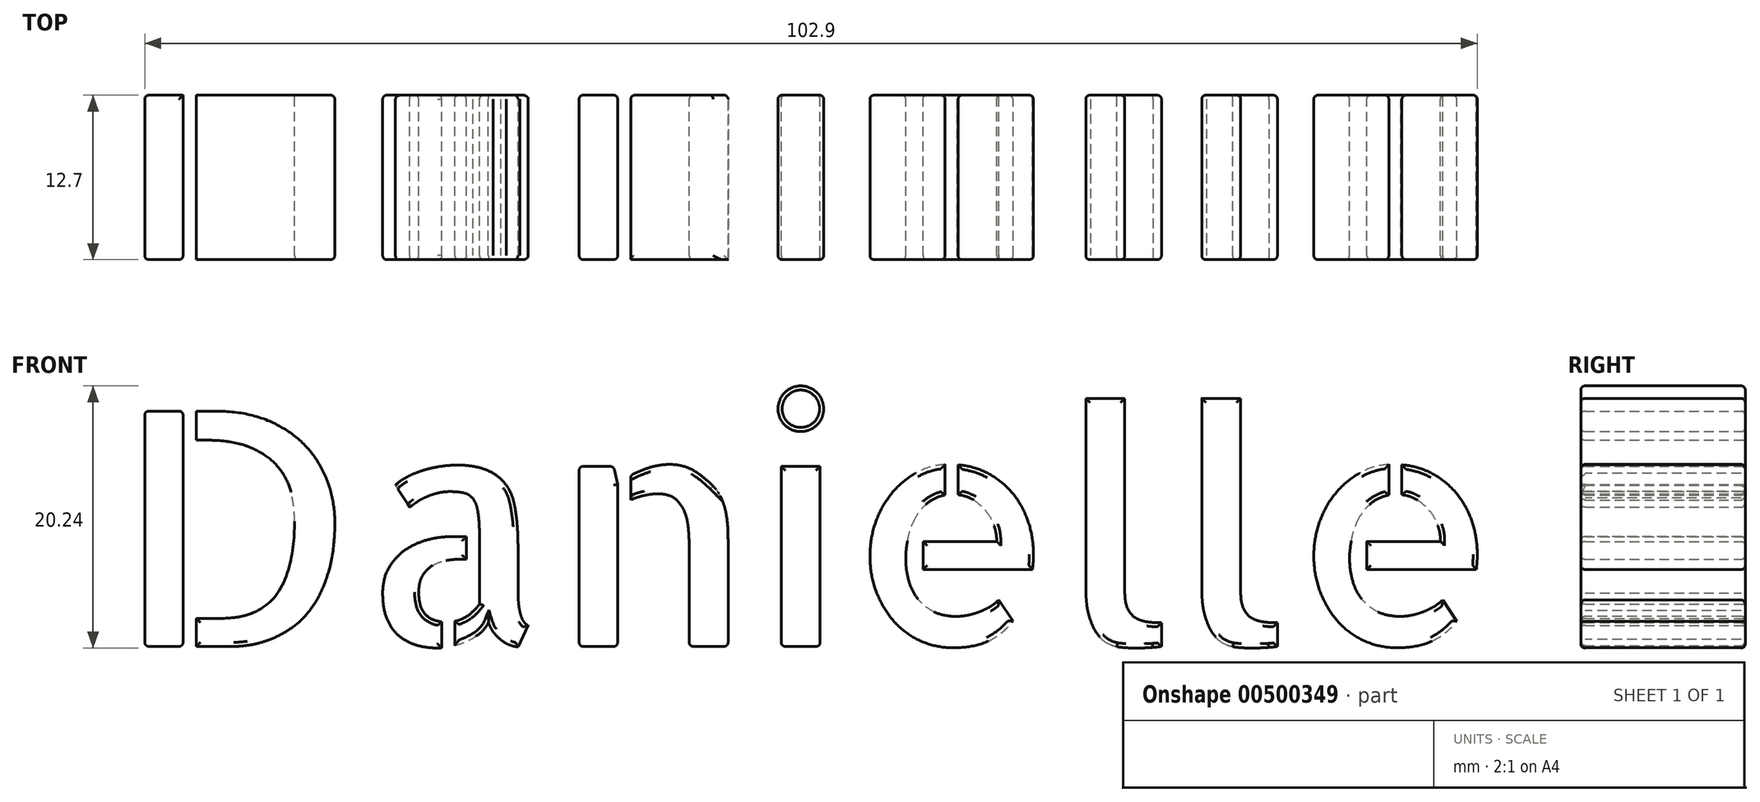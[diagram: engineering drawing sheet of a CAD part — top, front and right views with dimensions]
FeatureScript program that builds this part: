
annotation { "Feature Type Name" : "Feature", "Feature Type Description" : "" }
export const myFeature = defineFeature(function(context is Context, id is Id, definition is map)
    precondition{}
    {
        {
            var Q0;
            Q0=qCreatedBy(makeId("Front.planeOp"),FACE);
            var sketch = newSketch(context, id + "F0", { "sketchPlane" : qUnion([Q0])});
            skText(sketch, "E0", { "text": "Danielle", "fontName": "AllertaStencil-Regular.ttf"});
            const initialGuessF0  = {"E0": [-0.06588, 0.00923, 1, 0, 0.01818]};
            skSetInitialGuess(sketch, initialGuessF0);
            skSolve(sketch);
        }
        {
            var Q0;
            Q0 = qSketchRegion(id + "F0", true);
            extrude(context, id + "F1", {"entities" : qUnion([Q0]), "depth" : 12.7 * mm});
        }
        {
            var Q0;
            Q0=makeQuery(id+"F1.opExtrude","CAP_EDGE",EDGE,{"disambiguationData":[OSD([sQuery(id+"F0.wireOp",EDGE,"E0.sketch_text.stroke-3")])],"isStart":false});
            var Q1;
            Q1=makeQuery(id+"F1.opExtrude","CAP_EDGE",EDGE,{"disambiguationData":[OSD([sQuery(id+"F0.wireOp",EDGE,"E0.sketch_text.stroke-32")])],"isStart":false});
            var Q2;
            Q2=makeQuery(id+"F1.opExtrude","CAP_EDGE",EDGE,{"disambiguationData":[OSD([sQuery(id+"F0.wireOp",EDGE,"E0.sketch_text.stroke-60")])],"isStart":false});
            var Q3;
            Q3=makeQuery(id+"F1.opExtrude","CAP_EDGE",EDGE,{"disambiguationData":[OSD([sQuery(id+"F0.wireOp",EDGE,"E0.sketch_text.stroke-57")])],"isStart":false});
            var Q4;
            Q4=makeQuery(id+"F1.opExtrude","CAP_EDGE",EDGE,{"disambiguationData":[OSD([sQuery(id+"F0.wireOp",EDGE,"E0.sketch_text.stroke-56")])],"isStart":false});
            var Q5;
            Q5=makeQuery(id+"F1.opExtrude","CAP_EDGE",EDGE,{"disambiguationData":[OSD([sQuery(id+"F0.wireOp",EDGE,"E0.sketch_text.stroke-55")])],"isStart":false});
            var Q6;
            Q6=makeQuery(id+"F1.opExtrude","CAP_EDGE",EDGE,{"disambiguationData":[OSD([sQuery(id+"F0.wireOp",EDGE,"E0.sketch_text.stroke-52")])],"isStart":false});
            var Q7;
            Q7=makeQuery(id+"F1.opExtrude","CAP_EDGE",EDGE,{"disambiguationData":[OSD([sQuery(id+"F0.wireOp",EDGE,"E0.sketch_text.stroke-45")])],"isStart":false});
            var Q8;
            Q8=makeQuery(id+"F1.opExtrude","CAP_EDGE",EDGE,{"disambiguationData":[OSD([sQuery(id+"F0.wireOp",EDGE,"E0.sketch_text.stroke-49")])],"isStart":false});
            var Q9;
            Q9=makeQuery(id+"F1.opExtrude","CAP_EDGE",EDGE,{"disambiguationData":[OSD([sQuery(id+"F0.wireOp",EDGE,"E0.sketch_text.stroke-42")])],"isStart":false});
            var Q10;
            Q10=makeQuery(id+"F1.opExtrude","CAP_EDGE",EDGE,{"disambiguationData":[OSD([sQuery(id+"F0.wireOp",EDGE,"E0.sketch_text.stroke-28")])],"isStart":false});
            var Q11;
            Q11=makeQuery(id+"F1.opExtrude","CAP_FACE",FACE,{"disambiguationData":[OSD([sQuery(id+"F0.wireOp",EDGE,"E0.sketch_text.stroke-26"),sQuery(id+"F0.wireOp",EDGE,"E0.sketch_text.stroke-27"),sQuery(id+"F0.wireOp",EDGE,"E0.sketch_text.stroke-28"),sQuery(id+"F0.wireOp",EDGE,"E0.sketch_text.stroke-29"),sQuery(id+"F0.wireOp",EDGE,"E0.sketch_text.stroke-30"),sQuery(id+"F0.wireOp",EDGE,"E0.sketch_text.stroke-31"),sQuery(id+"F0.wireOp",EDGE,"E0.sketch_text.stroke-32"),sQuery(id+"F0.wireOp",EDGE,"E0.sketch_text.stroke-33"),sQuery(id+"F0.wireOp",EDGE,"E0.sketch_text.stroke-34"),sQuery(id+"F0.wireOp",EDGE,"E0.sketch_text.stroke-35"),sQuery(id+"F0.wireOp",EDGE,"E0.sketch_text.stroke-36"),sQuery(id+"F0.wireOp",EDGE,"E0.sketch_text.stroke-37"),sQuery(id+"F0.wireOp",EDGE,"E0.sketch_text.stroke-38"),sQuery(id+"F0.wireOp",EDGE,"E0.sketch_text.stroke-39"),sQuery(id+"F0.wireOp",EDGE,"E0.sketch_text.stroke-40"),sQuery(id+"F0.wireOp",EDGE,"E0.sketch_text.stroke-41"),sQuery(id+"F0.wireOp",EDGE,"E0.sketch_text.stroke-42"),sQuery(id+"F0.wireOp",EDGE,"E0.sketch_text.stroke-43"),sQuery(id+"F0.wireOp",EDGE,"E0.sketch_text.stroke-44")])],"isStart":false});
            var Q12;
            Q12=makeQuery(id+"F1.opExtrude","CAP_EDGE",EDGE,{"disambiguationData":[OSD([sQuery(id+"F0.wireOp",EDGE,"E0.sketch_text.stroke-83")])],"isStart":false});
            var Q13;
            Q13=makeQuery(id+"F1.opExtrude","CAP_EDGE",EDGE,{"disambiguationData":[OSD([sQuery(id+"F0.wireOp",EDGE,"E0.sketch_text.stroke-84")])],"isStart":false});
            var Q14;
            Q14=makeQuery(id+"F1.opExtrude","CAP_EDGE",EDGE,{"disambiguationData":[OSD([sQuery(id+"F0.wireOp",EDGE,"E0.sketch_text.stroke-9")])],"isStart":false});
            var Q15;
            Q15=makeQuery(id+"F1.opExtrude","CAP_EDGE",EDGE,{"disambiguationData":[OSD([sQuery(id+"F0.wireOp",EDGE,"E0.sketch_text.stroke-18")])],"isStart":false});
            var Q16;
            Q16=makeQuery(id+"F1.opExtrude","CAP_EDGE",EDGE,{"disambiguationData":[OSD([sQuery(id+"F0.wireOp",EDGE,"E0.sketch_text.stroke-15")])],"isStart":false});
            var Q17;
            Q17=makeQuery(id+"F1.opExtrude","CAP_EDGE",EDGE,{"disambiguationData":[OSD([sQuery(id+"F0.wireOp",EDGE,"E0.sketch_text.stroke-82")])],"isStart":false});
            var Q18;
            Q18=makeQuery(id+"F1.opExtrude","SWEPT_FACE",FACE,{"disambiguationData":[OSD([sQuery(id+"F0.wireOp",EDGE,"E0.sketch_text.stroke-85")])]});
            var Q19;
            Q19=makeQuery(id+"F1.opExtrude","CAP_EDGE",EDGE,{"disambiguationData":[OSD([sQuery(id+"F0.wireOp",EDGE,"E0.sketch_text.stroke-81")])],"isStart":false});
            var Q20;
            Q20=makeQuery(id+"F1.opExtrude","SWEPT_EDGE",EDGE,{"disambiguationData":[OSD([sQuery(id+"F0.wireOp",EDGE,"E0.sketch_text.stroke-100"),sQuery(id+"F0.wireOp",EDGE,"E0.sketch_text.stroke-101")])]});
            var Q21;
            Q21=makeQuery(id+"F1.opExtrude","CAP_EDGE",EDGE,{"disambiguationData":[OSD([sQuery(id+"F0.wireOp",EDGE,"E0.sketch_text.stroke-103")])],"isStart":false});
            var Q22;
            Q22=makeQuery(id+"F1.opExtrude","CAP_EDGE",EDGE,{"disambiguationData":[OSD([sQuery(id+"F0.wireOp",EDGE,"E0.sketch_text.stroke-98")])],"isStart":false});
            var Q23;
            Q23=makeQuery(id+"F1.opExtrude","CAP_EDGE",EDGE,{"disambiguationData":[OSD([sQuery(id+"F0.wireOp",EDGE,"E0.sketch_text.stroke-92")])],"isStart":false});
            var Q24;
            Q24=makeQuery(id+"F1.opExtrude","CAP_EDGE",EDGE,{"disambiguationData":[OSD([sQuery(id+"F0.wireOp",EDGE,"E0.sketch_text.stroke-106")])],"isStart":false});
            var Q25;
            Q25=makeQuery(id+"F1.opExtrude","CAP_EDGE",EDGE,{"disambiguationData":[OSD([sQuery(id+"F0.wireOp",EDGE,"E0.sketch_text.stroke-107")])],"isStart":false});
            var Q26;
            Q26=makeQuery(id+"F1.opExtrude","CAP_EDGE",EDGE,{"disambiguationData":[OSD([sQuery(id+"F0.wireOp",EDGE,"E0.sketch_text.stroke-110")])],"isStart":false});
            var Q27;
            Q27=makeQuery(id+"F1.opExtrude","CAP_FACE",FACE,{"disambiguationData":[OSD([sQuery(id+"F0.wireOp",EDGE,"E0.sketch_text.stroke-109"),sQuery(id+"F0.wireOp",EDGE,"E0.sketch_text.stroke-110"),sQuery(id+"F0.wireOp",EDGE,"E0.sketch_text.stroke-111"),sQuery(id+"F0.wireOp",EDGE,"E0.sketch_text.stroke-112"),sQuery(id+"F0.wireOp",EDGE,"E0.sketch_text.stroke-113"),sQuery(id+"F0.wireOp",EDGE,"E0.sketch_text.stroke-114"),sQuery(id+"F0.wireOp",EDGE,"E0.sketch_text.stroke-115"),sQuery(id+"F0.wireOp",EDGE,"E0.sketch_text.stroke-116")])],"isStart":false});
            var Q28;
            Q28=makeQuery(id+"F1.opExtrude","CAP_FACE",FACE,{"disambiguationData":[OSD([sQuery(id+"F0.wireOp",EDGE,"E0.sketch_text.stroke-130"),sQuery(id+"F0.wireOp",EDGE,"E0.sketch_text.stroke-131"),sQuery(id+"F0.wireOp",EDGE,"E0.sketch_text.stroke-132"),sQuery(id+"F0.wireOp",EDGE,"E0.sketch_text.stroke-133"),sQuery(id+"F0.wireOp",EDGE,"E0.sketch_text.stroke-134"),sQuery(id+"F0.wireOp",EDGE,"E0.sketch_text.stroke-135"),sQuery(id+"F0.wireOp",EDGE,"E0.sketch_text.stroke-136"),sQuery(id+"F0.wireOp",EDGE,"E0.sketch_text.stroke-137"),sQuery(id+"F0.wireOp",EDGE,"E0.sketch_text.stroke-138"),sQuery(id+"F0.wireOp",EDGE,"E0.sketch_text.stroke-139"),sQuery(id+"F0.wireOp",EDGE,"E0.sketch_text.stroke-140"),sQuery(id+"F0.wireOp",EDGE,"E0.sketch_text.stroke-141"),sQuery(id+"F0.wireOp",EDGE,"E0.sketch_text.stroke-142"),sQuery(id+"F0.wireOp",EDGE,"E0.sketch_text.stroke-143"),sQuery(id+"F0.wireOp",EDGE,"E0.sketch_text.stroke-144"),sQuery(id+"F0.wireOp",EDGE,"E0.sketch_text.stroke-145"),sQuery(id+"F0.wireOp",EDGE,"E0.sketch_text.stroke-146"),sQuery(id+"F0.wireOp",EDGE,"E0.sketch_text.stroke-147"),sQuery(id+"F0.wireOp",EDGE,"E0.sketch_text.stroke-148"),sQuery(id+"F0.wireOp",EDGE,"E0.sketch_text.stroke-149"),sQuery(id+"F0.wireOp",EDGE,"E0.sketch_text.stroke-150"),sQuery(id+"F0.wireOp",EDGE,"E0.sketch_text.stroke-151"),sQuery(id+"F0.wireOp",EDGE,"E0.sketch_text.stroke-152"),sQuery(id+"F0.wireOp",EDGE,"E0.sketch_text.stroke-153")])],"isStart":false});
            var Q29;
            Q29=makeQuery(id+"F1.opExtrude","CAP_FACE",FACE,{"disambiguationData":[OSD([sQuery(id+"F0.wireOp",EDGE,"E0.sketch_text.stroke-117"),sQuery(id+"F0.wireOp",EDGE,"E0.sketch_text.stroke-118"),sQuery(id+"F0.wireOp",EDGE,"E0.sketch_text.stroke-119"),sQuery(id+"F0.wireOp",EDGE,"E0.sketch_text.stroke-120"),sQuery(id+"F0.wireOp",EDGE,"E0.sketch_text.stroke-121"),sQuery(id+"F0.wireOp",EDGE,"E0.sketch_text.stroke-122"),sQuery(id+"F0.wireOp",EDGE,"E0.sketch_text.stroke-123"),sQuery(id+"F0.wireOp",EDGE,"E0.sketch_text.stroke-124"),sQuery(id+"F0.wireOp",EDGE,"E0.sketch_text.stroke-125"),sQuery(id+"F0.wireOp",EDGE,"E0.sketch_text.stroke-126"),sQuery(id+"F0.wireOp",EDGE,"E0.sketch_text.stroke-127"),sQuery(id+"F0.wireOp",EDGE,"E0.sketch_text.stroke-128"),sQuery(id+"F0.wireOp",EDGE,"E0.sketch_text.stroke-129")])],"isStart":false});
            var Q30;
            Q30=makeQuery(id+"F1.opExtrude","CAP_FACE",FACE,{"disambiguationData":[OSD([sQuery(id+"F0.wireOp",EDGE,"E0.sketch_text.stroke-0"),sQuery(id+"F0.wireOp",EDGE,"E0.sketch_text.stroke-1"),sQuery(id+"F0.wireOp",EDGE,"E0.sketch_text.stroke-2"),sQuery(id+"F0.wireOp",EDGE,"E0.sketch_text.stroke-3")])],"isStart":false});
            var Q31;
            Q31=makeQuery(id+"F1.opExtrude","SWEPT_FACE",FACE,{"disambiguationData":[OSD([sQuery(id+"F0.wireOp",EDGE,"E0.sketch_text.stroke-0")])]});
            var Q32;
            Q32=makeQuery(id+"F1.opExtrude","CAP_FACE",FACE,{"disambiguationData":[OSD([sQuery(id+"F0.wireOp",EDGE,"E0.sketch_text.stroke-154"),sQuery(id+"F0.wireOp",EDGE,"E0.sketch_text.stroke-155"),sQuery(id+"F0.wireOp",EDGE,"E0.sketch_text.stroke-156"),sQuery(id+"F0.wireOp",EDGE,"E0.sketch_text.stroke-157"),sQuery(id+"F0.wireOp",EDGE,"E0.sketch_text.stroke-158"),sQuery(id+"F0.wireOp",EDGE,"E0.sketch_text.stroke-159"),sQuery(id+"F0.wireOp",EDGE,"E0.sketch_text.stroke-160"),sQuery(id+"F0.wireOp",EDGE,"E0.sketch_text.stroke-161"),sQuery(id+"F0.wireOp",EDGE,"E0.sketch_text.stroke-162"),sQuery(id+"F0.wireOp",EDGE,"E0.sketch_text.stroke-163"),sQuery(id+"F0.wireOp",EDGE,"E0.sketch_text.stroke-164"),sQuery(id+"F0.wireOp",EDGE,"E0.sketch_text.stroke-165"),sQuery(id+"F0.wireOp",EDGE,"E0.sketch_text.stroke-166"),sQuery(id+"F0.wireOp",EDGE,"E0.sketch_text.stroke-167"),sQuery(id+"F0.wireOp",EDGE,"E0.sketch_text.stroke-168"),sQuery(id+"F0.wireOp",EDGE,"E0.sketch_text.stroke-169"),sQuery(id+"F0.wireOp",EDGE,"E0.sketch_text.stroke-170"),sQuery(id+"F0.wireOp",EDGE,"E0.sketch_text.stroke-171")])],"isStart":false});
            var Q33;
            Q33=makeQuery(id+"F1.opExtrude","CAP_FACE",FACE,{"disambiguationData":[OSD([sQuery(id+"F0.wireOp",EDGE,"E0.sketch_text.stroke-172"),sQuery(id+"F0.wireOp",EDGE,"E0.sketch_text.stroke-173"),sQuery(id+"F0.wireOp",EDGE,"E0.sketch_text.stroke-174"),sQuery(id+"F0.wireOp",EDGE,"E0.sketch_text.stroke-175"),sQuery(id+"F0.wireOp",EDGE,"E0.sketch_text.stroke-176"),sQuery(id+"F0.wireOp",EDGE,"E0.sketch_text.stroke-177"),sQuery(id+"F0.wireOp",EDGE,"E0.sketch_text.stroke-178"),sQuery(id+"F0.wireOp",EDGE,"E0.sketch_text.stroke-179"),sQuery(id+"F0.wireOp",EDGE,"E0.sketch_text.stroke-180"),sQuery(id+"F0.wireOp",EDGE,"E0.sketch_text.stroke-181"),sQuery(id+"F0.wireOp",EDGE,"E0.sketch_text.stroke-182"),sQuery(id+"F0.wireOp",EDGE,"E0.sketch_text.stroke-183"),sQuery(id+"F0.wireOp",EDGE,"E0.sketch_text.stroke-184"),sQuery(id+"F0.wireOp",EDGE,"E0.sketch_text.stroke-185"),sQuery(id+"F0.wireOp",EDGE,"E0.sketch_text.stroke-186"),sQuery(id+"F0.wireOp",EDGE,"E0.sketch_text.stroke-187"),sQuery(id+"F0.wireOp",EDGE,"E0.sketch_text.stroke-188"),sQuery(id+"F0.wireOp",EDGE,"E0.sketch_text.stroke-189")])],"isStart":false});
            var Q34;
            Q34=makeQuery(id+"F1.opExtrude","CAP_FACE",FACE,{"disambiguationData":[OSD([sQuery(id+"F0.wireOp",EDGE,"E0.sketch_text.stroke-203"),sQuery(id+"F0.wireOp",EDGE,"E0.sketch_text.stroke-204"),sQuery(id+"F0.wireOp",EDGE,"E0.sketch_text.stroke-205"),sQuery(id+"F0.wireOp",EDGE,"E0.sketch_text.stroke-206"),sQuery(id+"F0.wireOp",EDGE,"E0.sketch_text.stroke-207"),sQuery(id+"F0.wireOp",EDGE,"E0.sketch_text.stroke-208"),sQuery(id+"F0.wireOp",EDGE,"E0.sketch_text.stroke-209"),sQuery(id+"F0.wireOp",EDGE,"E0.sketch_text.stroke-210"),sQuery(id+"F0.wireOp",EDGE,"E0.sketch_text.stroke-211"),sQuery(id+"F0.wireOp",EDGE,"E0.sketch_text.stroke-212"),sQuery(id+"F0.wireOp",EDGE,"E0.sketch_text.stroke-213"),sQuery(id+"F0.wireOp",EDGE,"E0.sketch_text.stroke-214"),sQuery(id+"F0.wireOp",EDGE,"E0.sketch_text.stroke-215"),sQuery(id+"F0.wireOp",EDGE,"E0.sketch_text.stroke-216"),sQuery(id+"F0.wireOp",EDGE,"E0.sketch_text.stroke-217"),sQuery(id+"F0.wireOp",EDGE,"E0.sketch_text.stroke-218"),sQuery(id+"F0.wireOp",EDGE,"E0.sketch_text.stroke-219"),sQuery(id+"F0.wireOp",EDGE,"E0.sketch_text.stroke-220"),sQuery(id+"F0.wireOp",EDGE,"E0.sketch_text.stroke-221"),sQuery(id+"F0.wireOp",EDGE,"E0.sketch_text.stroke-222"),sQuery(id+"F0.wireOp",EDGE,"E0.sketch_text.stroke-223"),sQuery(id+"F0.wireOp",EDGE,"E0.sketch_text.stroke-224"),sQuery(id+"F0.wireOp",EDGE,"E0.sketch_text.stroke-225"),sQuery(id+"F0.wireOp",EDGE,"E0.sketch_text.stroke-226")])],"isStart":false});
            var Q35;
            Q35=makeQuery(id+"F1.opExtrude","CAP_FACE",FACE,{"disambiguationData":[OSD([sQuery(id+"F0.wireOp",EDGE,"E0.sketch_text.stroke-190"),sQuery(id+"F0.wireOp",EDGE,"E0.sketch_text.stroke-191"),sQuery(id+"F0.wireOp",EDGE,"E0.sketch_text.stroke-192"),sQuery(id+"F0.wireOp",EDGE,"E0.sketch_text.stroke-193"),sQuery(id+"F0.wireOp",EDGE,"E0.sketch_text.stroke-194"),sQuery(id+"F0.wireOp",EDGE,"E0.sketch_text.stroke-195"),sQuery(id+"F0.wireOp",EDGE,"E0.sketch_text.stroke-196"),sQuery(id+"F0.wireOp",EDGE,"E0.sketch_text.stroke-197"),sQuery(id+"F0.wireOp",EDGE,"E0.sketch_text.stroke-198"),sQuery(id+"F0.wireOp",EDGE,"E0.sketch_text.stroke-199"),sQuery(id+"F0.wireOp",EDGE,"E0.sketch_text.stroke-200"),sQuery(id+"F0.wireOp",EDGE,"E0.sketch_text.stroke-201"),sQuery(id+"F0.wireOp",EDGE,"E0.sketch_text.stroke-202")])],"isStart":false});
            var Q36;
            Q36=makeQuery(id+"F1.opExtrude","CAP_FACE",FACE,{"disambiguationData":[OSD([sQuery(id+"F0.wireOp",EDGE,"E0.sketch_text.stroke-105"),sQuery(id+"F0.wireOp",EDGE,"E0.sketch_text.stroke-106"),sQuery(id+"F0.wireOp",EDGE,"E0.sketch_text.stroke-107"),sQuery(id+"F0.wireOp",EDGE,"E0.sketch_text.stroke-108")])],"isStart":false});
            var Q37;
            Q37=makeQuery(id+"F1.opExtrude","CAP_FACE",FACE,{"disambiguationData":[OSD([sQuery(id+"F0.wireOp",EDGE,"E0.sketch_text.stroke-172"),sQuery(id+"F0.wireOp",EDGE,"E0.sketch_text.stroke-173"),sQuery(id+"F0.wireOp",EDGE,"E0.sketch_text.stroke-174"),sQuery(id+"F0.wireOp",EDGE,"E0.sketch_text.stroke-175"),sQuery(id+"F0.wireOp",EDGE,"E0.sketch_text.stroke-176"),sQuery(id+"F0.wireOp",EDGE,"E0.sketch_text.stroke-177"),sQuery(id+"F0.wireOp",EDGE,"E0.sketch_text.stroke-178"),sQuery(id+"F0.wireOp",EDGE,"E0.sketch_text.stroke-179"),sQuery(id+"F0.wireOp",EDGE,"E0.sketch_text.stroke-180"),sQuery(id+"F0.wireOp",EDGE,"E0.sketch_text.stroke-181"),sQuery(id+"F0.wireOp",EDGE,"E0.sketch_text.stroke-182"),sQuery(id+"F0.wireOp",EDGE,"E0.sketch_text.stroke-183"),sQuery(id+"F0.wireOp",EDGE,"E0.sketch_text.stroke-184"),sQuery(id+"F0.wireOp",EDGE,"E0.sketch_text.stroke-185"),sQuery(id+"F0.wireOp",EDGE,"E0.sketch_text.stroke-186"),sQuery(id+"F0.wireOp",EDGE,"E0.sketch_text.stroke-187"),sQuery(id+"F0.wireOp",EDGE,"E0.sketch_text.stroke-188"),sQuery(id+"F0.wireOp",EDGE,"E0.sketch_text.stroke-189")])],"isStart":true});
            var Q38;
            Q38=makeQuery(id+"F1.opExtrude","CAP_FACE",FACE,{"disambiguationData":[OSD([sQuery(id+"F0.wireOp",EDGE,"E0.sketch_text.stroke-154"),sQuery(id+"F0.wireOp",EDGE,"E0.sketch_text.stroke-155"),sQuery(id+"F0.wireOp",EDGE,"E0.sketch_text.stroke-156"),sQuery(id+"F0.wireOp",EDGE,"E0.sketch_text.stroke-157"),sQuery(id+"F0.wireOp",EDGE,"E0.sketch_text.stroke-158"),sQuery(id+"F0.wireOp",EDGE,"E0.sketch_text.stroke-159"),sQuery(id+"F0.wireOp",EDGE,"E0.sketch_text.stroke-160"),sQuery(id+"F0.wireOp",EDGE,"E0.sketch_text.stroke-161"),sQuery(id+"F0.wireOp",EDGE,"E0.sketch_text.stroke-162"),sQuery(id+"F0.wireOp",EDGE,"E0.sketch_text.stroke-163"),sQuery(id+"F0.wireOp",EDGE,"E0.sketch_text.stroke-164"),sQuery(id+"F0.wireOp",EDGE,"E0.sketch_text.stroke-165"),sQuery(id+"F0.wireOp",EDGE,"E0.sketch_text.stroke-166"),sQuery(id+"F0.wireOp",EDGE,"E0.sketch_text.stroke-167"),sQuery(id+"F0.wireOp",EDGE,"E0.sketch_text.stroke-168"),sQuery(id+"F0.wireOp",EDGE,"E0.sketch_text.stroke-169"),sQuery(id+"F0.wireOp",EDGE,"E0.sketch_text.stroke-170"),sQuery(id+"F0.wireOp",EDGE,"E0.sketch_text.stroke-171")])],"isStart":true});
            var Q39;
            Q39=makeQuery(id+"F1.opExtrude","CAP_FACE",FACE,{"disambiguationData":[OSD([sQuery(id+"F0.wireOp",EDGE,"E0.sketch_text.stroke-203"),sQuery(id+"F0.wireOp",EDGE,"E0.sketch_text.stroke-204"),sQuery(id+"F0.wireOp",EDGE,"E0.sketch_text.stroke-205"),sQuery(id+"F0.wireOp",EDGE,"E0.sketch_text.stroke-206"),sQuery(id+"F0.wireOp",EDGE,"E0.sketch_text.stroke-207"),sQuery(id+"F0.wireOp",EDGE,"E0.sketch_text.stroke-208"),sQuery(id+"F0.wireOp",EDGE,"E0.sketch_text.stroke-209"),sQuery(id+"F0.wireOp",EDGE,"E0.sketch_text.stroke-210"),sQuery(id+"F0.wireOp",EDGE,"E0.sketch_text.stroke-211"),sQuery(id+"F0.wireOp",EDGE,"E0.sketch_text.stroke-212"),sQuery(id+"F0.wireOp",EDGE,"E0.sketch_text.stroke-213"),sQuery(id+"F0.wireOp",EDGE,"E0.sketch_text.stroke-214"),sQuery(id+"F0.wireOp",EDGE,"E0.sketch_text.stroke-215"),sQuery(id+"F0.wireOp",EDGE,"E0.sketch_text.stroke-216"),sQuery(id+"F0.wireOp",EDGE,"E0.sketch_text.stroke-217"),sQuery(id+"F0.wireOp",EDGE,"E0.sketch_text.stroke-218"),sQuery(id+"F0.wireOp",EDGE,"E0.sketch_text.stroke-219"),sQuery(id+"F0.wireOp",EDGE,"E0.sketch_text.stroke-220"),sQuery(id+"F0.wireOp",EDGE,"E0.sketch_text.stroke-221"),sQuery(id+"F0.wireOp",EDGE,"E0.sketch_text.stroke-222"),sQuery(id+"F0.wireOp",EDGE,"E0.sketch_text.stroke-223"),sQuery(id+"F0.wireOp",EDGE,"E0.sketch_text.stroke-224"),sQuery(id+"F0.wireOp",EDGE,"E0.sketch_text.stroke-225"),sQuery(id+"F0.wireOp",EDGE,"E0.sketch_text.stroke-226")])],"isStart":true});
            var Q40;
            Q40=makeQuery(id+"F1.opExtrude","CAP_FACE",FACE,{"disambiguationData":[OSD([sQuery(id+"F0.wireOp",EDGE,"E0.sketch_text.stroke-190"),sQuery(id+"F0.wireOp",EDGE,"E0.sketch_text.stroke-191"),sQuery(id+"F0.wireOp",EDGE,"E0.sketch_text.stroke-192"),sQuery(id+"F0.wireOp",EDGE,"E0.sketch_text.stroke-193"),sQuery(id+"F0.wireOp",EDGE,"E0.sketch_text.stroke-194"),sQuery(id+"F0.wireOp",EDGE,"E0.sketch_text.stroke-195"),sQuery(id+"F0.wireOp",EDGE,"E0.sketch_text.stroke-196"),sQuery(id+"F0.wireOp",EDGE,"E0.sketch_text.stroke-197"),sQuery(id+"F0.wireOp",EDGE,"E0.sketch_text.stroke-198"),sQuery(id+"F0.wireOp",EDGE,"E0.sketch_text.stroke-199"),sQuery(id+"F0.wireOp",EDGE,"E0.sketch_text.stroke-200"),sQuery(id+"F0.wireOp",EDGE,"E0.sketch_text.stroke-201"),sQuery(id+"F0.wireOp",EDGE,"E0.sketch_text.stroke-202")])],"isStart":true});
            var Q41;
            Q41=makeQuery(id+"F1.opExtrude","CAP_FACE",FACE,{"disambiguationData":[OSD([sQuery(id+"F0.wireOp",EDGE,"E0.sketch_text.stroke-117"),sQuery(id+"F0.wireOp",EDGE,"E0.sketch_text.stroke-118"),sQuery(id+"F0.wireOp",EDGE,"E0.sketch_text.stroke-119"),sQuery(id+"F0.wireOp",EDGE,"E0.sketch_text.stroke-120"),sQuery(id+"F0.wireOp",EDGE,"E0.sketch_text.stroke-121"),sQuery(id+"F0.wireOp",EDGE,"E0.sketch_text.stroke-122"),sQuery(id+"F0.wireOp",EDGE,"E0.sketch_text.stroke-123"),sQuery(id+"F0.wireOp",EDGE,"E0.sketch_text.stroke-124"),sQuery(id+"F0.wireOp",EDGE,"E0.sketch_text.stroke-125"),sQuery(id+"F0.wireOp",EDGE,"E0.sketch_text.stroke-126"),sQuery(id+"F0.wireOp",EDGE,"E0.sketch_text.stroke-127"),sQuery(id+"F0.wireOp",EDGE,"E0.sketch_text.stroke-128"),sQuery(id+"F0.wireOp",EDGE,"E0.sketch_text.stroke-129")])],"isStart":true});
            var Q42;
            Q42=makeQuery(id+"F1.opExtrude","CAP_FACE",FACE,{"disambiguationData":[OSD([sQuery(id+"F0.wireOp",EDGE,"E0.sketch_text.stroke-130"),sQuery(id+"F0.wireOp",EDGE,"E0.sketch_text.stroke-131"),sQuery(id+"F0.wireOp",EDGE,"E0.sketch_text.stroke-132"),sQuery(id+"F0.wireOp",EDGE,"E0.sketch_text.stroke-133"),sQuery(id+"F0.wireOp",EDGE,"E0.sketch_text.stroke-134"),sQuery(id+"F0.wireOp",EDGE,"E0.sketch_text.stroke-135"),sQuery(id+"F0.wireOp",EDGE,"E0.sketch_text.stroke-136"),sQuery(id+"F0.wireOp",EDGE,"E0.sketch_text.stroke-137"),sQuery(id+"F0.wireOp",EDGE,"E0.sketch_text.stroke-138"),sQuery(id+"F0.wireOp",EDGE,"E0.sketch_text.stroke-139"),sQuery(id+"F0.wireOp",EDGE,"E0.sketch_text.stroke-140"),sQuery(id+"F0.wireOp",EDGE,"E0.sketch_text.stroke-141"),sQuery(id+"F0.wireOp",EDGE,"E0.sketch_text.stroke-142"),sQuery(id+"F0.wireOp",EDGE,"E0.sketch_text.stroke-143"),sQuery(id+"F0.wireOp",EDGE,"E0.sketch_text.stroke-144"),sQuery(id+"F0.wireOp",EDGE,"E0.sketch_text.stroke-145"),sQuery(id+"F0.wireOp",EDGE,"E0.sketch_text.stroke-146"),sQuery(id+"F0.wireOp",EDGE,"E0.sketch_text.stroke-147"),sQuery(id+"F0.wireOp",EDGE,"E0.sketch_text.stroke-148"),sQuery(id+"F0.wireOp",EDGE,"E0.sketch_text.stroke-149"),sQuery(id+"F0.wireOp",EDGE,"E0.sketch_text.stroke-150"),sQuery(id+"F0.wireOp",EDGE,"E0.sketch_text.stroke-151"),sQuery(id+"F0.wireOp",EDGE,"E0.sketch_text.stroke-152"),sQuery(id+"F0.wireOp",EDGE,"E0.sketch_text.stroke-153")])],"isStart":true});
            var Q43;
            Q43=makeQuery(id+"F1.opExtrude","CAP_FACE",FACE,{"disambiguationData":[OSD([sQuery(id+"F0.wireOp",EDGE,"E0.sketch_text.stroke-105"),sQuery(id+"F0.wireOp",EDGE,"E0.sketch_text.stroke-106"),sQuery(id+"F0.wireOp",EDGE,"E0.sketch_text.stroke-107"),sQuery(id+"F0.wireOp",EDGE,"E0.sketch_text.stroke-108")])],"isStart":true});
            var Q44;
            Q44=makeQuery(id+"F1.opExtrude","CAP_FACE",FACE,{"disambiguationData":[OSD([sQuery(id+"F0.wireOp",EDGE,"E0.sketch_text.stroke-109"),sQuery(id+"F0.wireOp",EDGE,"E0.sketch_text.stroke-110"),sQuery(id+"F0.wireOp",EDGE,"E0.sketch_text.stroke-111"),sQuery(id+"F0.wireOp",EDGE,"E0.sketch_text.stroke-112"),sQuery(id+"F0.wireOp",EDGE,"E0.sketch_text.stroke-113"),sQuery(id+"F0.wireOp",EDGE,"E0.sketch_text.stroke-114"),sQuery(id+"F0.wireOp",EDGE,"E0.sketch_text.stroke-115"),sQuery(id+"F0.wireOp",EDGE,"E0.sketch_text.stroke-116")])],"isStart":true});
            var Q45;
            Q45=makeQuery(id+"F1.opExtrude","CAP_FACE",FACE,{"disambiguationData":[OSD([sQuery(id+"F0.wireOp",EDGE,"E0.sketch_text.stroke-86"),sQuery(id+"F0.wireOp",EDGE,"E0.sketch_text.stroke-87"),sQuery(id+"F0.wireOp",EDGE,"E0.sketch_text.stroke-88"),sQuery(id+"F0.wireOp",EDGE,"E0.sketch_text.stroke-89"),sQuery(id+"F0.wireOp",EDGE,"E0.sketch_text.stroke-90"),sQuery(id+"F0.wireOp",EDGE,"E0.sketch_text.stroke-91"),sQuery(id+"F0.wireOp",EDGE,"E0.sketch_text.stroke-92"),sQuery(id+"F0.wireOp",EDGE,"E0.sketch_text.stroke-93"),sQuery(id+"F0.wireOp",EDGE,"E0.sketch_text.stroke-94"),sQuery(id+"F0.wireOp",EDGE,"E0.sketch_text.stroke-95"),sQuery(id+"F0.wireOp",EDGE,"E0.sketch_text.stroke-96"),sQuery(id+"F0.wireOp",EDGE,"E0.sketch_text.stroke-97"),sQuery(id+"F0.wireOp",EDGE,"E0.sketch_text.stroke-98"),sQuery(id+"F0.wireOp",EDGE,"E0.sketch_text.stroke-99"),sQuery(id+"F0.wireOp",EDGE,"E0.sketch_text.stroke-100"),sQuery(id+"F0.wireOp",EDGE,"E0.sketch_text.stroke-101"),sQuery(id+"F0.wireOp",EDGE,"E0.sketch_text.stroke-102"),sQuery(id+"F0.wireOp",EDGE,"E0.sketch_text.stroke-103"),sQuery(id+"F0.wireOp",EDGE,"E0.sketch_text.stroke-104")])],"isStart":true});
            var Q46;
            Q46=makeQuery(id+"F1.opExtrude","CAP_FACE",FACE,{"disambiguationData":[OSD([sQuery(id+"F0.wireOp",EDGE,"E0.sketch_text.stroke-81"),sQuery(id+"F0.wireOp",EDGE,"E0.sketch_text.stroke-82"),sQuery(id+"F0.wireOp",EDGE,"E0.sketch_text.stroke-83"),sQuery(id+"F0.wireOp",EDGE,"E0.sketch_text.stroke-84"),sQuery(id+"F0.wireOp",EDGE,"E0.sketch_text.stroke-85")])],"isStart":true});
            var Q47;
            Q47=makeQuery(id+"F1.opExtrude","CAP_FACE",FACE,{"disambiguationData":[OSD([sQuery(id+"F0.wireOp",EDGE,"E0.sketch_text.stroke-45"),sQuery(id+"F0.wireOp",EDGE,"E0.sketch_text.stroke-46"),sQuery(id+"F0.wireOp",EDGE,"E0.sketch_text.stroke-47"),sQuery(id+"F0.wireOp",EDGE,"E0.sketch_text.stroke-48"),sQuery(id+"F0.wireOp",EDGE,"E0.sketch_text.stroke-49"),sQuery(id+"F0.wireOp",EDGE,"E0.sketch_text.stroke-50"),sQuery(id+"F0.wireOp",EDGE,"E0.sketch_text.stroke-51"),sQuery(id+"F0.wireOp",EDGE,"E0.sketch_text.stroke-52"),sQuery(id+"F0.wireOp",EDGE,"E0.sketch_text.stroke-53"),sQuery(id+"F0.wireOp",EDGE,"E0.sketch_text.stroke-54"),sQuery(id+"F0.wireOp",EDGE,"E0.sketch_text.stroke-55"),sQuery(id+"F0.wireOp",EDGE,"E0.sketch_text.stroke-56"),sQuery(id+"F0.wireOp",EDGE,"E0.sketch_text.stroke-57"),sQuery(id+"F0.wireOp",EDGE,"E0.sketch_text.stroke-58"),sQuery(id+"F0.wireOp",EDGE,"E0.sketch_text.stroke-59"),sQuery(id+"F0.wireOp",EDGE,"E0.sketch_text.stroke-60"),sQuery(id+"F0.wireOp",EDGE,"E0.sketch_text.stroke-61"),sQuery(id+"F0.wireOp",EDGE,"E0.sketch_text.stroke-62"),sQuery(id+"F0.wireOp",EDGE,"E0.sketch_text.stroke-63"),sQuery(id+"F0.wireOp",EDGE,"E0.sketch_text.stroke-64"),sQuery(id+"F0.wireOp",EDGE,"E0.sketch_text.stroke-65"),sQuery(id+"F0.wireOp",EDGE,"E0.sketch_text.stroke-66"),sQuery(id+"F0.wireOp",EDGE,"E0.sketch_text.stroke-67"),sQuery(id+"F0.wireOp",EDGE,"E0.sketch_text.stroke-68"),sQuery(id+"F0.wireOp",EDGE,"E0.sketch_text.stroke-69"),sQuery(id+"F0.wireOp",EDGE,"E0.sketch_text.stroke-70"),sQuery(id+"F0.wireOp",EDGE,"E0.sketch_text.stroke-71"),sQuery(id+"F0.wireOp",EDGE,"E0.sketch_text.stroke-72"),sQuery(id+"F0.wireOp",EDGE,"E0.sketch_text.stroke-73"),sQuery(id+"F0.wireOp",EDGE,"E0.sketch_text.stroke-74"),sQuery(id+"F0.wireOp",EDGE,"E0.sketch_text.stroke-75"),sQuery(id+"F0.wireOp",EDGE,"E0.sketch_text.stroke-76"),sQuery(id+"F0.wireOp",EDGE,"E0.sketch_text.stroke-77"),sQuery(id+"F0.wireOp",EDGE,"E0.sketch_text.stroke-78"),sQuery(id+"F0.wireOp",EDGE,"E0.sketch_text.stroke-79"),sQuery(id+"F0.wireOp",EDGE,"E0.sketch_text.stroke-80")])],"isStart":true});
            var Q48;
            Q48=makeQuery(id+"F1.opExtrude","CAP_FACE",FACE,{"disambiguationData":[OSD([sQuery(id+"F0.wireOp",EDGE,"E0.sketch_text.stroke-26"),sQuery(id+"F0.wireOp",EDGE,"E0.sketch_text.stroke-27"),sQuery(id+"F0.wireOp",EDGE,"E0.sketch_text.stroke-28"),sQuery(id+"F0.wireOp",EDGE,"E0.sketch_text.stroke-29"),sQuery(id+"F0.wireOp",EDGE,"E0.sketch_text.stroke-30"),sQuery(id+"F0.wireOp",EDGE,"E0.sketch_text.stroke-31"),sQuery(id+"F0.wireOp",EDGE,"E0.sketch_text.stroke-32"),sQuery(id+"F0.wireOp",EDGE,"E0.sketch_text.stroke-33"),sQuery(id+"F0.wireOp",EDGE,"E0.sketch_text.stroke-34"),sQuery(id+"F0.wireOp",EDGE,"E0.sketch_text.stroke-35"),sQuery(id+"F0.wireOp",EDGE,"E0.sketch_text.stroke-36"),sQuery(id+"F0.wireOp",EDGE,"E0.sketch_text.stroke-37"),sQuery(id+"F0.wireOp",EDGE,"E0.sketch_text.stroke-38"),sQuery(id+"F0.wireOp",EDGE,"E0.sketch_text.stroke-39"),sQuery(id+"F0.wireOp",EDGE,"E0.sketch_text.stroke-40"),sQuery(id+"F0.wireOp",EDGE,"E0.sketch_text.stroke-41"),sQuery(id+"F0.wireOp",EDGE,"E0.sketch_text.stroke-42"),sQuery(id+"F0.wireOp",EDGE,"E0.sketch_text.stroke-43"),sQuery(id+"F0.wireOp",EDGE,"E0.sketch_text.stroke-44")])],"isStart":true});
            var Q49;
            Q49=makeQuery(id+"F1.opExtrude","CAP_EDGE",EDGE,{"disambiguationData":[OSD([sQuery(id+"F0.wireOp",EDGE,"E0.sketch_text.stroke-3")])],"isStart":true});
            var Q50;
            Q50=makeQuery(id+"F1.opExtrude","SWEPT_FACE",FACE,{"disambiguationData":[OSD([sQuery(id+"F0.wireOp",EDGE,"E0.sketch_text.stroke-83")])]});
            var Q51;
            Q51=makeQuery(id+"F1.opExtrude","SWEPT_FACE",FACE,{"disambiguationData":[OSD([sQuery(id+"F0.wireOp",EDGE,"E0.sketch_text.stroke-92")])]});
            var Q52;
            Q52=makeQuery(id+"F1.opExtrude","SWEPT_FACE",FACE,{"disambiguationData":[OSD([sQuery(id+"F0.wireOp",EDGE,"E0.sketch_text.stroke-105")])]});
            var Q53;
            Q53=makeQuery(id+"F1.opExtrude","SWEPT_FACE",FACE,{"disambiguationData":[OSD([sQuery(id+"F0.wireOp",EDGE,"E0.sketch_text.stroke-2")])]});
            var Q54;
            Q54=makeQuery(id+"F1.opExtrude","CAP_EDGE",EDGE,{"disambiguationData":[OSD([sQuery(id+"F0.wireOp",EDGE,"E0.sketch_text.stroke-6")])],"isStart":true});
            fillet(context, id + "F2", {"entities" : qUnion([Q0, Q1, Q2, Q3, Q4, Q5, Q6, Q7, Q8, Q9, Q10, Q11, Q12, Q13, Q14, Q15, Q16, Q17, Q18, Q19, Q20, Q21, Q22, Q23, Q24, Q25, Q26, Q27, Q28, Q29, Q30, Q31, Q32, Q33, Q34, Q35, Q36, Q37, Q38, Q39, Q40, Q41, Q42, Q43, Q44, Q45, Q46, Q47, Q48, Q49, Q50, Q51, Q52, Q53, Q54]), "radius" : 0.32 * mm, "tangentPropagation" : true, "allowEdgeOverflow" : false});
        }
    });
